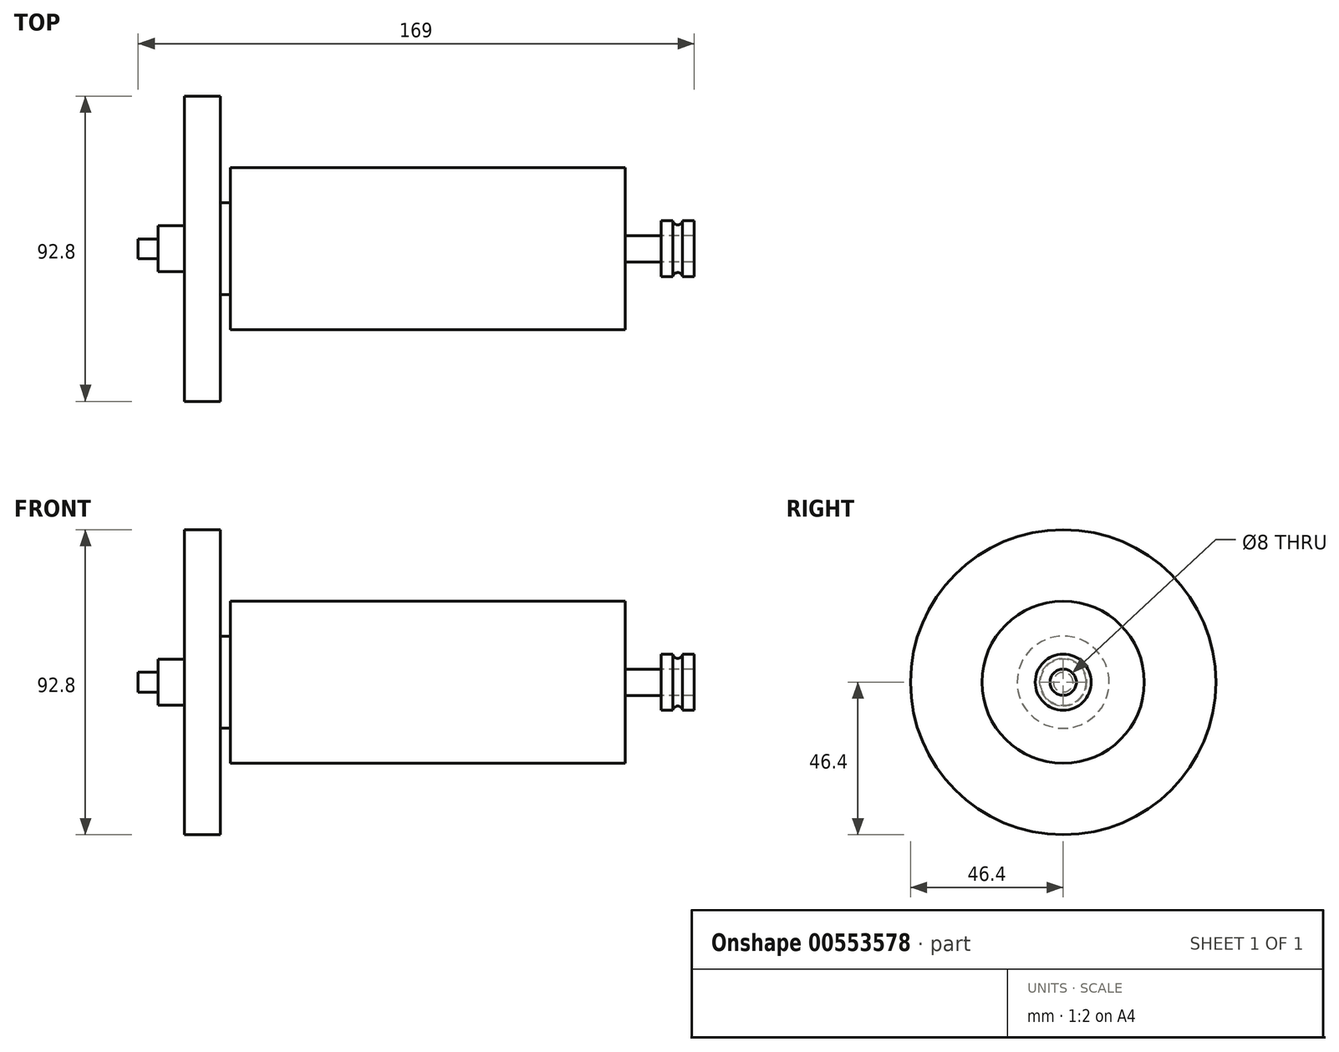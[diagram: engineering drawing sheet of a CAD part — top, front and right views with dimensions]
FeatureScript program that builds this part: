
annotation { "Feature Type Name" : "Feature", "Feature Type Description" : "" }
export const myFeature = defineFeature(function(context is Context, id is Id, definition is map)
    precondition{}
    {
        {
            var Q0;
            Q0=qCreatedBy(makeId("Right.planeOp"),FACE);
            var sketch = newSketch(context, id + "F0", { "sketchPlane" : qUnion([Q0])});
            skCircle(sketch, "E0", {"center": v(0, 0) * mm, "radius": 24.65 * mm});
            skSolve(sketch);
        }
        {
            var Q0;
            Q0 = qSketchRegion(id + "F0", true);
            extrude(context, id + "F1", {"entities" : qUnion([Q0]), "depth" : 120 * mm, "offsetDistance" : 25.4 * mm});
        }
        {
            var Q0;
            Q0=makeQuery(id+"F1.opExtrude","CAP_FACE",FACE,{"disambiguationData":[OSD([sQuery(id+"F0.wireOp",EDGE,"E0")])],"isStart":false});
            var sketch = newSketch(context, id + "F2", { "sketchPlane" : qUnion([Q0])});
            skCircle(sketch, "E1", {"center": v(0, 0) * mm, "radius": 4 * mm});
            skSolve(sketch);
        }
        {
            var Q0;
            Q0 = qSketchRegion(id + "F2", true);
            extrude(context, id + "F3", {"entities" : qUnion([Q0]), "operationType" : NewBodyOperationType.ADD, "depth" : 21 * mm, "offsetDistance" : 25.4 * mm});
        }
        {
            var Q0;
            Q0=makeQuery(id+"F1.opExtrude","CAP_FACE",FACE,{"disambiguationData":[OSD([sQuery(id+"F0.wireOp",EDGE,"E0")])],"isStart":true});
            var sketch = newSketch(context, id + "F4", { "sketchPlane" : qUnion([Q0])});
            skCircle(sketch, "E2", {"center": v(0, 0) * mm, "radius": 14 * mm});
            skSolve(sketch);
        }
        {
            var Q0;
            Q0=makeQuery(id+"F4.imprint","IMPRINT",FACE,{"disambiguationData":[TD([[makeQuery(id+"F4.imprint","IMPRINT",EDGE,{"derivedFrom":sQuery(id+"F4.wireOp",EDGE,"E2")}),1.0]])]});
            extrude(context, id + "F5", {"entities" : qUnion([Q0]), "operationType" : NewBodyOperationType.ADD, "depth" : 3 * mm, "offsetDistance" : 25.4 * mm});
        }
        {
            var Q0;
            Q0=makeQuery(id+"F5.opExtrude","CAP_FACE",FACE,{"disambiguationData":[OSD([sQuery(id+"F4.wireOp",EDGE,"E2")])],"isStart":false});
            var sketch = newSketch(context, id + "F6", { "sketchPlane" : qUnion([Q0])});
            skCircle(sketch, "E3", {"center": v(0, 0) * mm, "radius": 46.4 * mm});
            skSolve(sketch);
        }
        {
            var Q0;
            Q0=makeQuery(id+"F6.imprint","IMPRINT",FACE,{"disambiguationData":[TD([[makeQuery(id+"F6.imprint","IMPRINT",EDGE,{"derivedFrom":sQuery(id+"F6.wireOp",EDGE,"E3")}),1.0]])]});
            var Q1;
            Q1=makeQuery(id+"F6.imprint","IMPRINT",FACE,{"disambiguationData":[TD([[makeQuery(id+"F6.imprint","IMPRINT",EDGE,{"derivedFrom":makeQuery(id+"F5.opExtrude","CAP_EDGE",EDGE,{"disambiguationData":[OSD([sQuery(id+"F4.wireOp",EDGE,"E2")])],"isStart":false})}),1.0]])]});
            extrude(context, id + "F7", {"entities" : qUnion([Q0, Q1]), "depth" : 11 * mm, "offsetDistance" : 25.4 * mm});
        }
        {
            var Q0;
            Q0=makeQuery(id+"F7.opExtrude","CAP_FACE",FACE,{"disambiguationData":[OSD([sQuery(id+"F6.wireOp",EDGE,"E3")])],"isStart":false});
            var sketch = newSketch(context, id + "F8", { "sketchPlane" : qUnion([Q0])});
            skCircle(sketch, "E4", {"center": v(0, 0) * mm, "radius": 7 * mm});
            skSolve(sketch);
        }
        {
            var Q0;
            Q0=makeQuery(id+"F8.imprint","IMPRINT",FACE,{"disambiguationData":[TD([[makeQuery(id+"F8.imprint","IMPRINT",EDGE,{"derivedFrom":sQuery(id+"F8.wireOp",EDGE,"E4")}),1.0]])]});
            extrude(context, id + "F9", {"entities" : qUnion([Q0]), "operationType" : NewBodyOperationType.ADD, "depth" : 8 * mm, "offsetDistance" : 25.4 * mm});
        }
        {
            var Q0;
            Q0=makeQuery(id+"F9.opExtrude","CAP_FACE",FACE,{"disambiguationData":[OSD([sQuery(id+"F8.wireOp",EDGE,"E4")])],"isStart":false});
            var sketch = newSketch(context, id + "F10", { "sketchPlane" : qUnion([Q0])});
            skCircle(sketch, "E5", {"center": v(0, 0) * mm, "radius": 3 * mm});
            skSolve(sketch);
        }
        {
            var Q0;
            Q0=makeQuery(id+"F10.imprint","IMPRINT",FACE,{"disambiguationData":[TD([[makeQuery(id+"F10.imprint","IMPRINT",EDGE,{"derivedFrom":sQuery(id+"F10.wireOp",EDGE,"E5")}),1.0]])]});
            extrude(context, id + "F11", {"entities" : qUnion([Q0]), "operationType" : NewBodyOperationType.ADD, "depth" : 6 * mm, "offsetDistance" : 25.4 * mm});
        }
        {
            var Q0;
            Q0=makeQuery(id+"F3.opExtrude","CAP_FACE",FACE,{"disambiguationData":[OSD([sQuery(id+"F2.wireOp",EDGE,"E1")])],"isStart":false});
            var sketch = newSketch(context, id + "F12", { "sketchPlane" : qUnion([Q0])});
            skCircle(sketch, "E6", {"center": v(0, 0) * mm, "radius": 4 * mm});
            skCircle(sketch, "E7", {"center": v(0, 0) * mm, "radius": 8.5 * mm});
            skSolve(sketch);
        }
        {
            var Q0;
            Q0=makeQuery(id+"F12.imprint","IMPRINT",FACE,{"disambiguationData":[TD([[makeQuery(id+"F12.imprint","IMPRINT",EDGE,{"derivedFrom":sQuery(id+"F12.wireOp",EDGE,"E6")}),-1.0]])]});
            extrude(context, id + "F13", {"entities" : qUnion([Q0]), "oppositeDirection" : true, "depth" : 10 * mm, "offsetDistance" : 25 * mm});
        }
        {
            var Q0;
            Q0=qCreatedBy(makeId("Top.planeOp"),FACE);
            var sketch = newSketch(context, id + "F14", { "sketchPlane" : qUnion([Q0])});
            skLineSegment(sketch, "E8", {"start": v(0, 0) * mm, "end": v(502.96, 0) * mm});
            skSolve(sketch);
        }
        {
            var Q0;
            Q0=qCreatedBy(makeId("Top.planeOp"),FACE);
            var sketch = newSketch(context, id + "F15", { "sketchPlane" : qUnion([Q0])});
            skCircle(sketch, "E9", {"center": v(136, 8.75) * mm, "radius": 1.5 * mm});
            skSolve(sketch);
        }
        {
            var Q0;
            Q0 = qSketchRegion(id + "F15", true);
            var Q1;
            Q1=sQuery(id+"F14.wireOp",EDGE,"E8");
            revolve(context, id + "F16", {"operationType" : NewBodyOperationType.REMOVE, "entities" : qUnion([Q0]), "axis" : qUnion([Q1]), "revolveType" : RevolveType.FULL});
        }
    });
